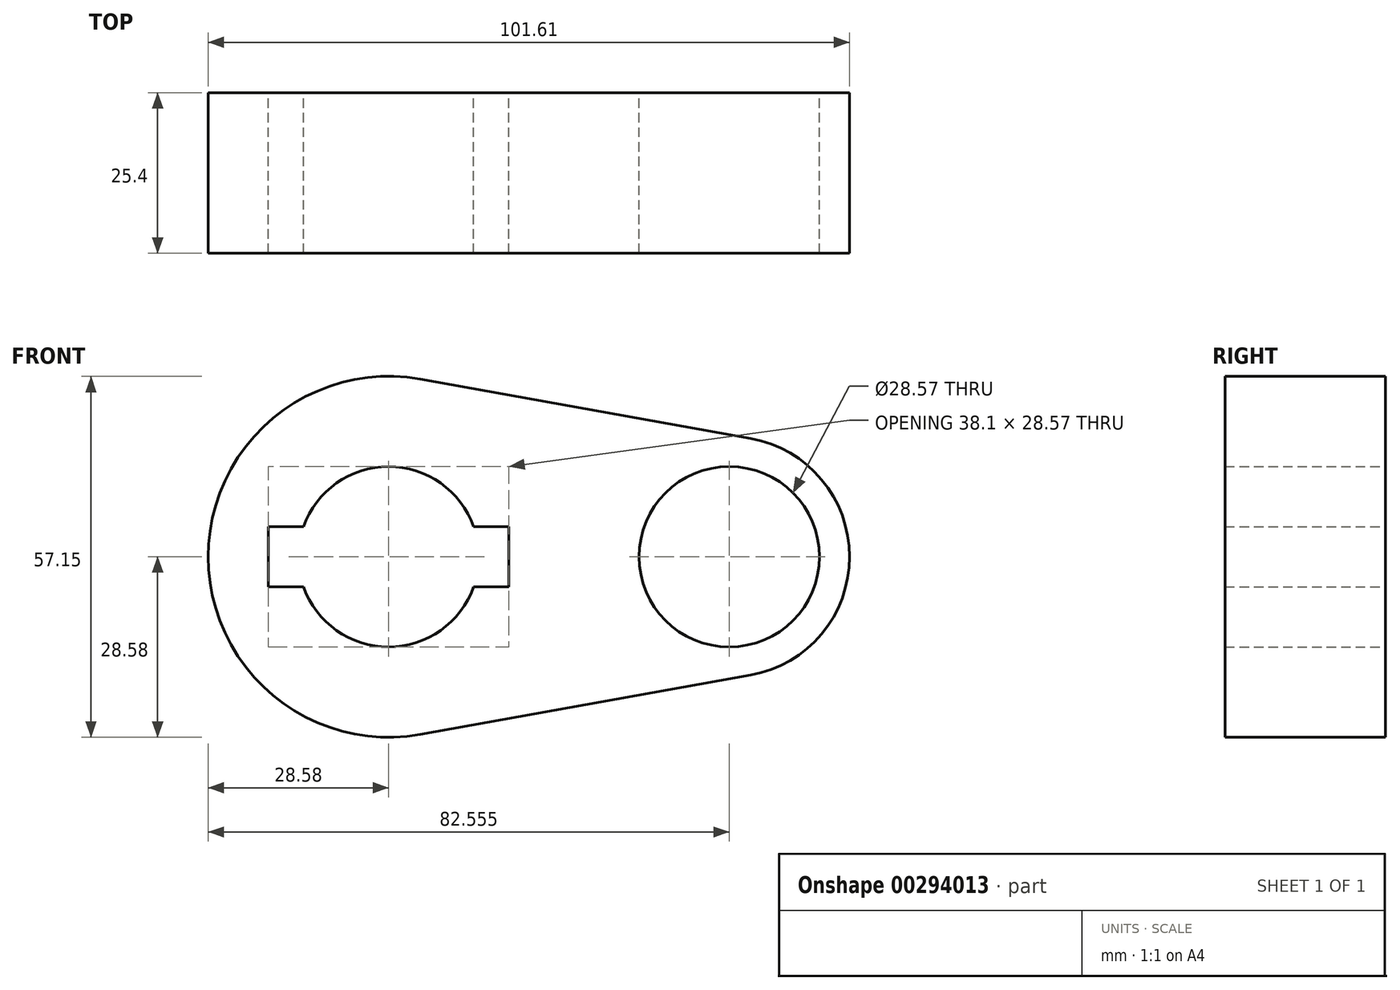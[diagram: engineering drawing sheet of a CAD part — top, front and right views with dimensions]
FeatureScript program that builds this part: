
annotation { "Feature Type Name" : "Feature", "Feature Type Description" : "" }
export const myFeature = defineFeature(function(context is Context, id is Id, definition is map)
    precondition{}
    {
        {
            var Q0;
            Q0=qCreatedBy(makeId("Front.planeOp"),FACE);
            var sketch = newSketch(context, id + "F0", { "sketchPlane" : qUnion([Q0])});
            skCircle(sketch, "E0", {"center": v(0, 0) * mm, "radius": 28.58 * mm});
            skCircle(sketch, "E1", {"center": v(53.97, 0) * mm, "radius": 19.05 * mm});
            skLineSegment(sketch, "E2", {"start": v(5.04, 28.13) * mm, "end": v(57.34, 18.75) * mm});
            skLineSegment(sketch, "E3", {"start": v(5.04, -28.13) * mm, "end": v(57.34, -18.75) * mm});
            skCircle(sketch, "E4", {"center": v(0, 0) * mm, "radius": 14.29 * mm});
            skCircle(sketch, "E5", {"center": v(53.97, 0) * mm, "radius": 14.29 * mm});
            skLineSegment(sketch, "E6.bottom", {"start": v(-19.05, -4.76) * mm, "end": v(19.05, -4.76) * mm});
            skLineSegment(sketch, "E6.top", {"start": v(-19.05, 4.76) * mm, "end": v(19.05, 4.76) * mm});
            skLineSegment(sketch, "E6.left", {"start": v(-19.05, -4.76) * mm, "end": v(-19.05, 4.76) * mm});
            skLineSegment(sketch, "E6.right", {"start": v(19.05, -4.76) * mm, "end": v(19.05, 4.76) * mm});
            skSolve(sketch);
        }
        {
            var Q0;
            Q0 = qSketchRegion(id + "F0", true);
            extrude(context, id + "F1", {"entities" : qUnion([Q0]), "depth" : 25.4 * mm});
        }
    });
